# Revit family: Moment Wooden Leg Square
name_source: partatom
category: Furniture
revit_build: Autodesk Revit 2016 (Build: 20151007_0715(x64)
units: mm (PartAtom-declared; Revit-internal decimal feet)

## family parameters
Always vertical = Yes
Cut with Voids When Loaded = No
OmniClass Number = 23.40.20.00
OmniClass Title = General Furniture and Specialties
Room Calculation Point = No
Shared = No
Work Plane-Based = No

## types (4) — shared parameters
Assembly Code = E2020200
Foot = Gresham - Black Plastic
Frame = Gresham - Silver Metal
Manufacturer = Gresham Office Furniture
Range = MOMENT
Table Top = Gresham - White MFC
URL = www.gof.co.uk

## per-type parameters (varying)
| type | Product Code | Width |
| 1000 x 1000 | MSTR1010 | 1000 mm  [stored 3.28084 ft] |
| 1200 x 1200 | MSTR1212 | 1200 mm |
| 1400 x 1400 | MSTR1414 | 1400 mm  [stored 4.59318 ft] |
| 1600 x 1600 | MSTR1616 | 1600 mm  [stored 5.24934 ft] |

note: [stored X ft] marks values corroborated as IEEE doubles in the binary element streams (Revit-internal decimal feet)

## geometry (parser evidence)
native form markers: Blend x2, Sweep x6
no freeform markers — native parametric forms only
